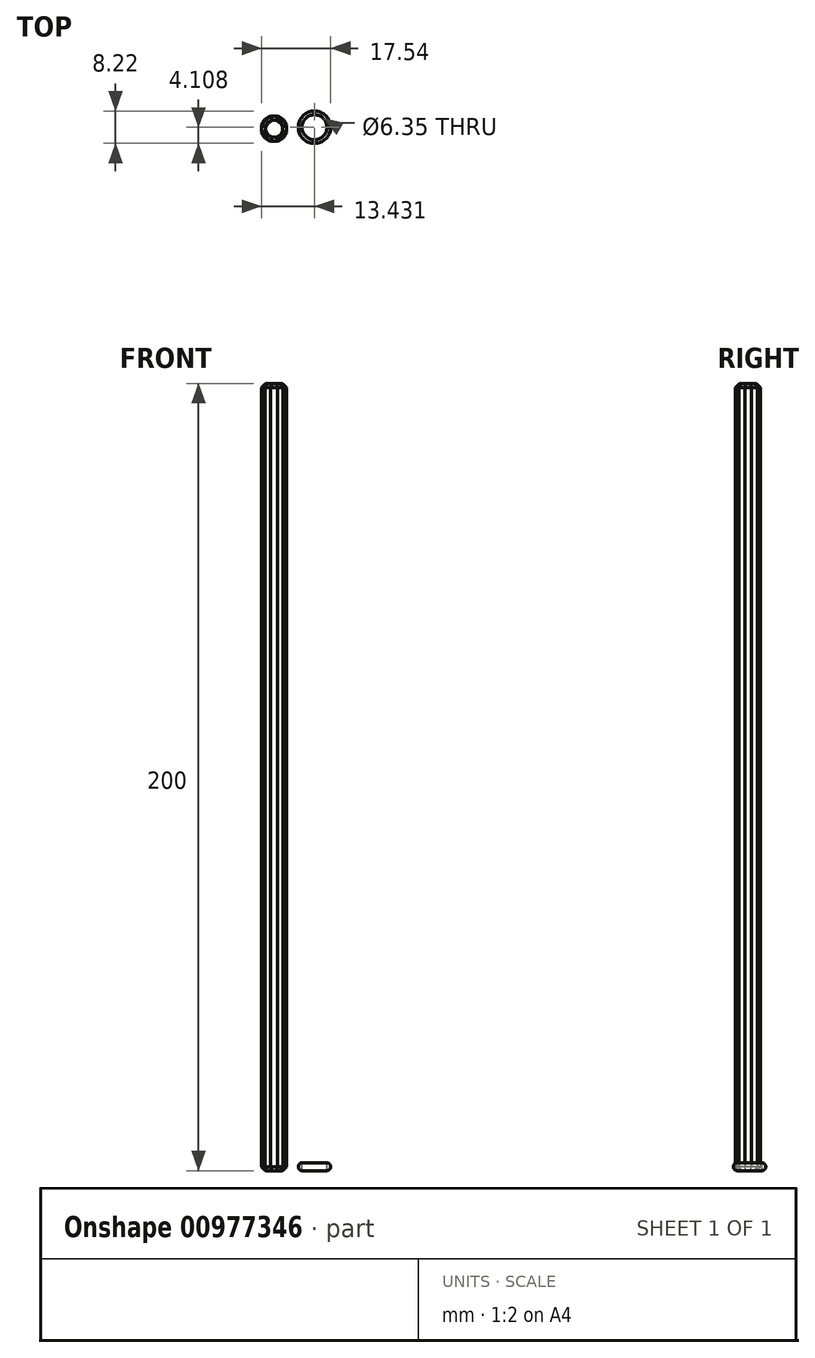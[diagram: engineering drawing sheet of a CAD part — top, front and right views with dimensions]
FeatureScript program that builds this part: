
annotation { "Feature Type Name" : "Feature", "Feature Type Description" : "" }
export const myFeature = defineFeature(function(context is Context, id is Id, definition is map)
    precondition{}
    {
        {
            var Q0;
            Q0=qCreatedBy(makeId("Top.planeOp"),FACE);
            var sketch = newSketch(context, id + "F0", { "sketchPlane" : qUnion([Q0])});
            skCircle(sketch, "E0.cCircle", {"center": v(-37.6, 27.53) * mm, "radius": 3.17 * mm, "construction": true});
            skLineSegment(sketch, "E0.0", {"start": v(-38.45, 30.7) * mm, "end": v(-36.75, 30.7) * mm});
            skLineSegment(sketch, "E0.1", {"start": v(-36.75, 30.7) * mm, "end": v(-35.28, 29.85) * mm});
            skLineSegment(sketch, "E0.2", {"start": v(-35.28, 29.85) * mm, "end": v(-34.43, 28.38) * mm});
            skLineSegment(sketch, "E0.3", {"start": v(-34.43, 28.38) * mm, "end": v(-34.43, 26.68) * mm});
            skLineSegment(sketch, "E0.4", {"start": v(-34.43, 26.68) * mm, "end": v(-35.28, 25.2) * mm});
            skLineSegment(sketch, "E0.5", {"start": v(-35.28, 25.2) * mm, "end": v(-36.75, 24.35) * mm});
            skLineSegment(sketch, "E0.6", {"start": v(-36.75, 24.35) * mm, "end": v(-38.45, 24.35) * mm});
            skLineSegment(sketch, "E0.7", {"start": v(-38.45, 24.35) * mm, "end": v(-39.92, 25.2) * mm});
            skLineSegment(sketch, "E0.8", {"start": v(-39.92, 25.2) * mm, "end": v(-40.77, 26.68) * mm});
            skLineSegment(sketch, "E0.9", {"start": v(-40.77, 26.68) * mm, "end": v(-40.77, 28.38) * mm});
            skLineSegment(sketch, "E0.10", {"start": v(-40.77, 28.38) * mm, "end": v(-39.92, 29.85) * mm});
            skLineSegment(sketch, "E0.11", {"start": v(-39.92, 29.85) * mm, "end": v(-38.45, 30.7) * mm});
            skPoint(sketch, "E0.0.midPoint", {"position": v(-37.6, 30.7) * mm});
            skSolve(sketch);
        }
        {
            var Q0;
            Q0=makeQuery(id+"F0.imprint","IMPRINT",FACE,{"disambiguationData":[TD([[makeQuery(id+"F0.imprint","IMPRINT",EDGE,{"derivedFrom":sQuery(id+"F0.wireOp",EDGE,"E0.0")}),-1.0]])]});
            extrude(context, id + "F1", {"entities" : qUnion([Q0]), "depth" : 200 * mm, "offsetDistance" : 25 * mm});
        }
        {
            var Q0;
            Q0=makeQuery(id+"F1.opExtrude","CAP_FACE",FACE,{"disambiguationData":[OSD([sQuery(id+"F0.wireOp",EDGE,"E0.0"),sQuery(id+"F0.wireOp",EDGE,"E0.1"),sQuery(id+"F0.wireOp",EDGE,"E0.2"),sQuery(id+"F0.wireOp",EDGE,"E0.3"),sQuery(id+"F0.wireOp",EDGE,"E0.4"),sQuery(id+"F0.wireOp",EDGE,"E0.5"),sQuery(id+"F0.wireOp",EDGE,"E0.6"),sQuery(id+"F0.wireOp",EDGE,"E0.7"),sQuery(id+"F0.wireOp",EDGE,"E0.8"),sQuery(id+"F0.wireOp",EDGE,"E0.9"),sQuery(id+"F0.wireOp",EDGE,"E0.10"),sQuery(id+"F0.wireOp",EDGE,"E0.11")])],"isStart":true});
            chamfer(context, id + "F2", {"entities" : qUnion([Q0]), "width" : 1 * mm, "tangentPropagation" : true});
        }
        {
            var Q0;
            Q0=makeQuery(id+"F1.opExtrude","CAP_FACE",FACE,{"disambiguationData":[OSD([sQuery(id+"F0.wireOp",EDGE,"E0.0"),sQuery(id+"F0.wireOp",EDGE,"E0.1"),sQuery(id+"F0.wireOp",EDGE,"E0.2"),sQuery(id+"F0.wireOp",EDGE,"E0.3"),sQuery(id+"F0.wireOp",EDGE,"E0.4"),sQuery(id+"F0.wireOp",EDGE,"E0.5"),sQuery(id+"F0.wireOp",EDGE,"E0.6"),sQuery(id+"F0.wireOp",EDGE,"E0.7"),sQuery(id+"F0.wireOp",EDGE,"E0.8"),sQuery(id+"F0.wireOp",EDGE,"E0.9"),sQuery(id+"F0.wireOp",EDGE,"E0.10"),sQuery(id+"F0.wireOp",EDGE,"E0.11")])],"isStart":false});
            chamfer(context, id + "F3", {"entities" : qUnion([Q0]), "width" : 1 * mm, "tangentPropagation" : true});
        }
        {
            var Q0;
            Q0=qCreatedBy(makeId("Top.planeOp"),FACE);
            var sketch = newSketch(context, id + "F4", { "sketchPlane" : qUnion([Q0])});
            skCircle(sketch, "E1", {"center": v(-27.34, 27.9) * mm, "radius": 4.1 * mm});
            skSolve(sketch);
        }
        {
            var Q0;
            Q0=qCreatedBy(makeId("Top.planeOp"),FACE);
            var sketch = newSketch(context, id + "F5", { "sketchPlane" : qUnion([Q0])});
            skCircle(sketch, "E2", {"center": v(-27.34, 27.91) * mm, "radius": 2.5 * mm});
            skSolve(sketch);
        }
        {
            var Q0;
            Q0=makeQuery(id+"F4.imprint","IMPRINT",FACE,{"disambiguationData":[TD([[makeQuery(id+"F4.imprint","IMPRINT",EDGE,{"derivedFrom":sQuery(id+"F4.wireOp",EDGE,"E1")}),1.0]])]});
            var Q1;
            Q1=sQuery(id+"F4.wireOp",EDGE,"E1");
            var Q2;
            Q2=sQuery(id+"F5.wireOp",EDGE,"E2");
            extrude(context, id + "F6", {"entities" : qUnion([Q0]), "surfaceEntities" : qUnion([Q1, Q2]), "depth" : 2 * mm, "offsetDistance" : 25 * mm});
        }
        {
            var Q0;
            Q0=makeQuery(id+"F6.opExtrude","CAP_FACE",FACE,{"disambiguationData":[OSD([sQuery(id+"F4.wireOp",EDGE,"E1")])],"isStart":false});
            var sketch = newSketch(context, id + "F7", { "sketchPlane" : qUnion([Q0])});
            skCircle(sketch, "E3", {"center": v(-27.34, 27.9) * mm, "radius": 3.17 * mm});
            skSolve(sketch);
        }
        {
            var Q0;
            Q0 = qSketchRegion(id + "F7", true);
            extrude(context, id + "F8", {"entities" : qUnion([Q0]), "operationType" : NewBodyOperationType.REMOVE, "oppositeDirection" : true, "depth" : 25 * mm, "offsetDistance" : 25 * mm});
        }
        {
            var Q0;
            Q0=makeQuery(id+"F6.opExtrude","CAP_EDGE",EDGE,{"disambiguationData":[OSD([sQuery(id+"F4.wireOp",EDGE,"E1")])],"isStart":false});
            var Q1;
            Q1=makeQuery(id+"F6.opExtrude","CAP_EDGE",EDGE,{"disambiguationData":[OSD([sQuery(id+"F4.wireOp",EDGE,"E1")])],"isStart":true});
            fillet(context, id + "F9", {"entities" : qUnion([Q0, Q1]), "radius" : 1 * mm, "tangentPropagation" : true, "allowEdgeOverflow" : false});
        }
    });
